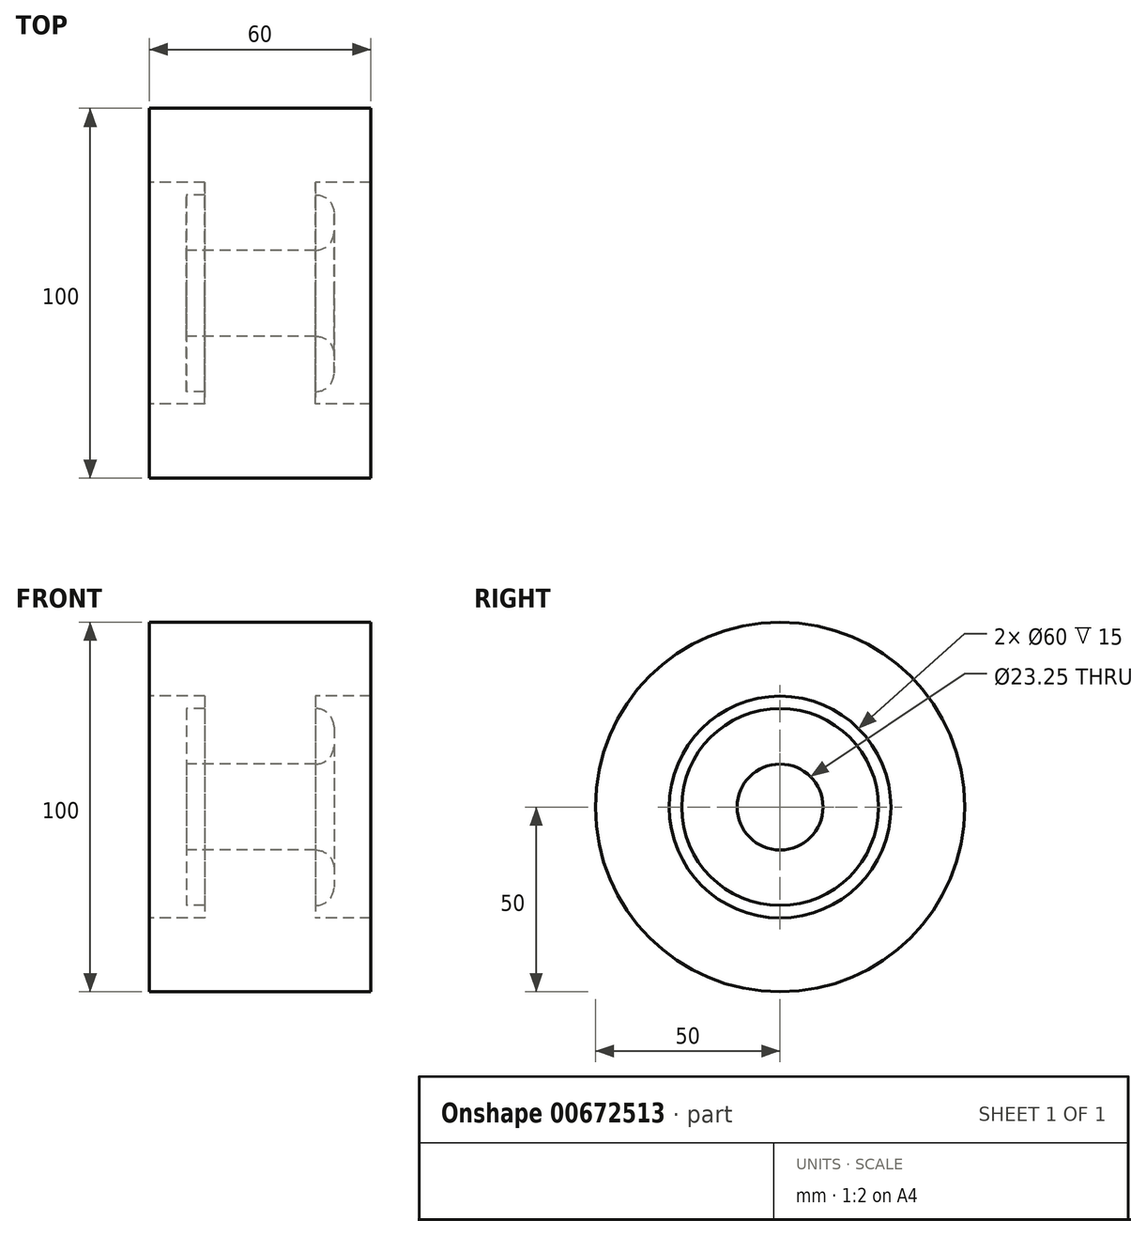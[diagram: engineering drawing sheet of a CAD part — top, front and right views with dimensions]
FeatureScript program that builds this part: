
annotation { "Feature Type Name" : "Feature", "Feature Type Description" : "" }
export const myFeature = defineFeature(function(context is Context, id is Id, definition is map)
    precondition{}
    {
        {
            var Q0;
            Q0=qCreatedBy(makeId("Front.planeOp"),FACE);
            var sketch = newSketch(context, id + "F0", { "sketchPlane" : qUnion([Q0])});
            skLineSegment(sketch, "E0", {"start": v(0, 0) * mm, "end": v(0, 50) * mm, "construction": true});
            skLineSegment(sketch, "E1", {"start": v(0, 11.63) * mm, "end": v(-20, 11.63) * mm});
            skLineSegment(sketch, "E2", {"start": v(-20, 11.63) * mm, "end": v(-20, 26.63) * mm});
            skLineSegment(sketch, "E3", {"start": v(-20, 26.63) * mm, "end": v(-15, 26.63) * mm});
            skLineSegment(sketch, "E4", {"start": v(-15, 26.63) * mm, "end": v(-15, 30) * mm});
            skLineSegment(sketch, "E5", {"start": v(-15, 30) * mm, "end": v(-30, 30) * mm});
            skLineSegment(sketch, "E6", {"start": v(-30, 30) * mm, "end": v(-30, 50) * mm});
            skLineSegment(sketch, "E7", {"start": v(-30, 50) * mm, "end": v(0, 50) * mm});
            skLineSegment(sketch, "E8", {"start": v(0, 0) * mm, "end": v(61.59, 0) * mm, "construction": true});
            skLineSegment(sketch, "E9.MirrorCS", {"start": v(30, 50) * mm, "end": v(0, 50) * mm});
            skLineSegment(sketch, "E10.MirrorCS", {"start": v(30, 30) * mm, "end": v(30, 50) * mm});
            skLineSegment(sketch, "E11.MirrorCS", {"start": v(15, 30) * mm, "end": v(30, 30) * mm});
            skLineSegment(sketch, "E12.MirrorCS", {"start": v(15, 26.63) * mm, "end": v(15, 30) * mm});
            skLineSegment(sketch, "E13.MirrorCS", {"start": v(20, 26.63) * mm, "end": v(15, 26.63) * mm});
            skLineSegment(sketch, "E14.MirrorCS", {"start": v(20, 11.63) * mm, "end": v(20, 26.63) * mm});
            skLineSegment(sketch, "E15.MirrorCS", {"start": v(0, 11.63) * mm, "end": v(20, 11.63) * mm});
            skSolve(sketch);
        }
        {
            var Q0;
            Q0=makeQuery(id+"F0.imprint","IMPRINT",FACE,{"disambiguationData":[TD([[makeQuery(id+"F0.imprint","IMPRINT",EDGE,{"derivedFrom":sQuery(id+"F0.wireOp",EDGE,"E1")}),-1.0]])]});
            var Q1;
            Q1=sQuery(id+"F0.wireOp",EDGE,"E8");
            revolve(context, id + "F1", {"entities" : qUnion([Q0]), "axis" : qUnion([Q1]), "revolveType" : RevolveType.FULL});
        }
        {
            var Q0;
            Q0=makeQuery(id+"F1.opRevolve","SWEPT_FACE",FACE,{"disambiguationData":[OSD([sQuery(id+"F0.wireOp",EDGE,"E14.MirrorCS")])]});
            fillet(context, id + "F2", {"entities" : qUnion([Q0]), "radius" : 5 * mm, "tangentPropagation" : true, "allowEdgeOverflow" : false});
        }
    });
